# Revit family: CVD
name_source: partatom
category: Mechanical Equipment
units: mm (PartAtom-declared; Revit-internal decimal feet)

## family parameters
Always vertical = Yes
Cut with Voids When Loaded = No
Part Type = Normal
Room Calculation Point = No
Round Connector Dimension = Use Radius
Shared = No
Work Plane-Based = No

## types (7) — shared parameters
0 = 0' - 0"
1" = 0' - 1"
1.5 = 0' - 1 1/2"
2" = 0' - 2"
2' = 2' - 0"
3" = 0' - 3"
3/16 = 0' - 0 3/16"
4" = 0' - 4"
E = 0' - 1 5/16"
Manufacturer = Loren Cook Company
Model = CVD
ONE EIGTH = 0' - 0 1/8"
THREE QUARTER = 0' - 0 3/4"
T_SQ = 2' - 8"
T_SQ/2 = 1' - 4"
Type Comments = Centri-Vane All Aluminum Inline Centrifugal Blower Direct Drive
URL = www.lorencook.com

## per-type parameters (varying)
| type | (A/2)+E | (C/2)-E | (F/2)-1" | (G/2)-1" | A | A/2 | B | B/2 | C | C/2 | D | F | F/2 | G | G/2 |
| 8_CVD | 0' - 5 5/16" | 0' - 5 13/32" | 0' - 4 5/8" | 0' - 4 1/8" | 0' - 8" | 0' - 4" | 1' - 1 1/4" | 0' - 6 5/8" | 1' - 1 7/16" | 0' - 6 23/32" | 0' - 7" | 0' - 11 1/4" | 0' - 5 5/8" | 0' - 10 1/4" | 0' - 5 1/8" |
| 10_CVD | 0' - 6 5/16" | 0' - 6 25/32" | 0' - 5 1/2" | 0' - 5 1/8" | 0' - 10" | 0' - 5" | 1' - 3" | 0' - 7 1/2" | 1' - 4 3/16" | 0' - 8 3/32" | 0' - 8 11/16" | 1' - 1" | 0' - 6 1/2" | 1' - 0 1/4" | 0' - 6 1/8" |
| 12_CVD | 0' - 7 5/16" | 0' - 8 5/16" | 0' - 6 9/16" | 0' - 6 1/16" | 1' - 0" | 0' - 6" | 1' - 5 1/8" | 0' - 8 9/16" | 1' - 7 1/4" | 0' - 9 5/8" | 0' - 9 15/16" | 1' - 3 1/8" | 0' - 7 9/16" | 1' - 2 1/8" | 0' - 7 1/16" |
| 14_CVD | 0' - 8 5/16" | 0' - 9 11/16" | 0' - 7 9/16" | 0' - 7 1/8" | 1' - 2" | 0' - 7" | 1' - 7 1/8" | 0' - 9 9/16" | 1' - 10" | 0' - 11" | 0' - 11 7/16" | 1' - 5 1/8" | 0' - 8 9/16" | 1' - 4 1/4" | 0' - 8 1/8" |
| 16_CVD | 0' - 9 5/16" | 0' - 11 1/8" | 0' - 8 25/32" | 0' - 8 1/8" | 1' - 4" | 0' - 8" | 1' - 9 9/16" | 0' - 10 25/32" | 2' - 0 7/8" | 1' - 0 7/16" | 1' - 0 11/16" | 1' - 7 9/16" | 0' - 9 25/32" | 1' - 6 1/4" | 0' - 9 1/8" |
| 18_CVD | 0' - 10 5/16" | 1' - 0 9/16" | 0' - 10 1/4" | 0' - 9 3/16" | 1' - 6" | 0' - 9" | 2' - 0 1/2" | 1' - 0 1/4" | 2' - 3 3/4" | 1' - 1 7/8" | 1' - 2" | 1' - 10 1/2" | 0' - 11 1/4" | 1' - 8 3/8" | 0' - 10 3/16" |
| 20_CVD | 0' - 11 5/16" | 1' - 1 15/16" | 0' - 11 3/16" | 0' - 10 1/4" | 1' - 8" | 0' - 10" | 2' - 2 3/8" | 1' - 1 3/16" | 2' - 6 1/2" | 1' - 3 1/4" | 1' - 3 3/4" | 2' - 0 3/8" | 1' - 0 3/16" | 1' - 10 1/2" | 0' - 11 1/4" |

## geometry (parser evidence)
native form markers: Sweep x2
no freeform markers — native parametric forms only
